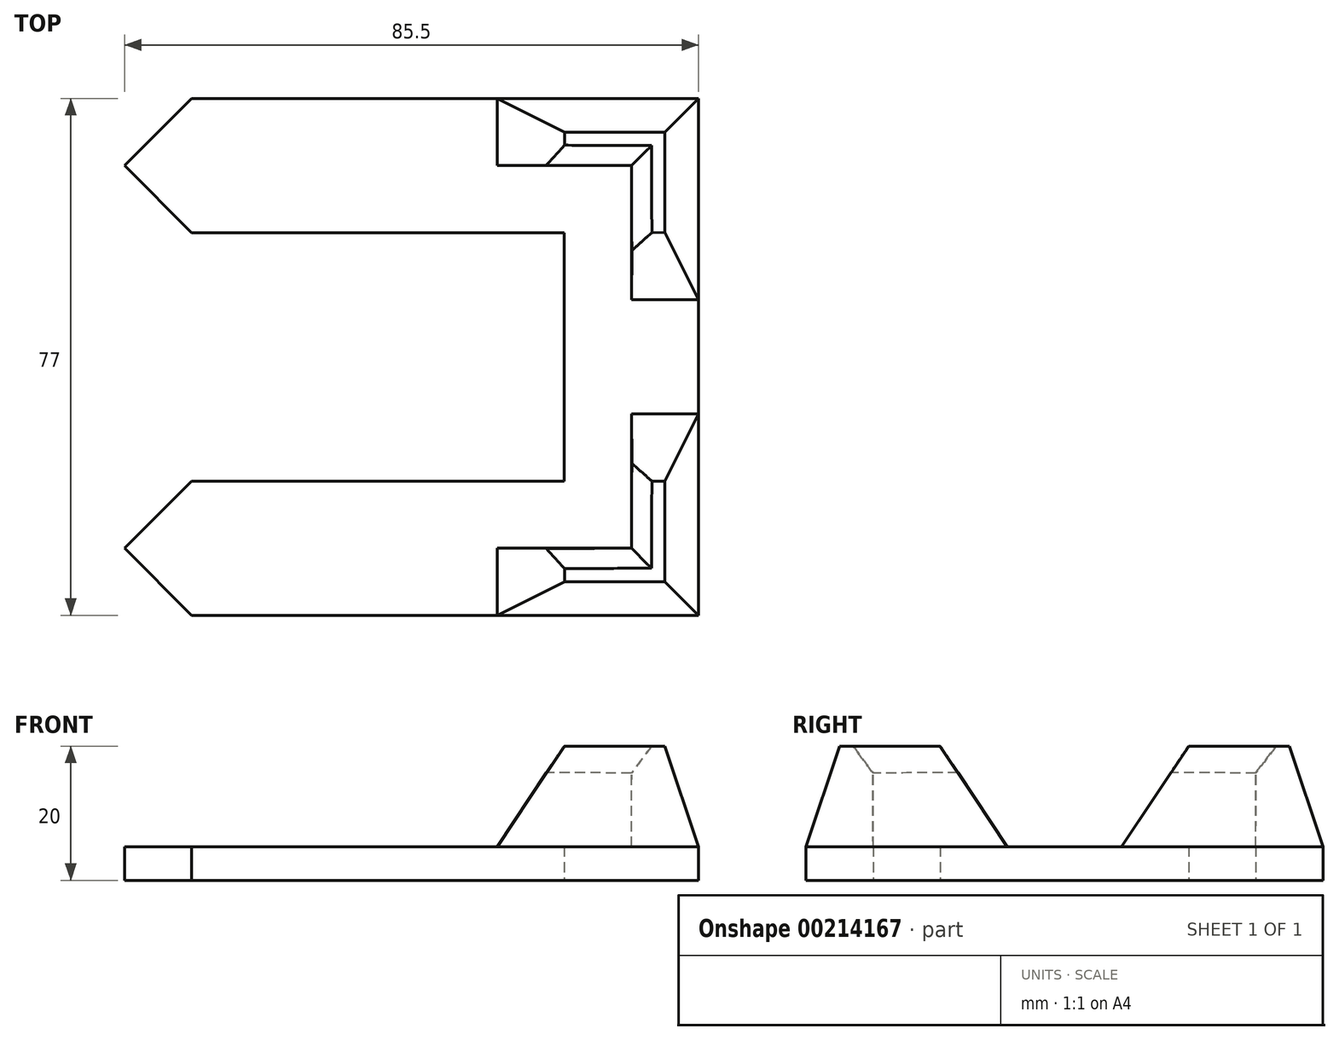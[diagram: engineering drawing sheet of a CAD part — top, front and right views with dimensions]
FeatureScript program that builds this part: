
annotation { "Feature Type Name" : "Feature", "Feature Type Description" : "" }
export const myFeature = defineFeature(function(context is Context, id is Id, definition is map)
    precondition{}
    {
        {
            var Q0;
            Q0=qCreatedBy(makeId("Top.planeOp"),FACE);
            var sketch = newSketch(context, id + "F0", { "sketchPlane" : qUnion([Q0])});
            skLineSegment(sketch, "E0.bottom", {"start": v(75.5, -28.5) * mm, "end": v(-75.5, -28.5) * mm, "construction": true});
            skLineSegment(sketch, "E0.top", {"start": v(75.5, 28.5) * mm, "end": v(-75.5, 28.5) * mm, "construction": true});
            skLineSegment(sketch, "E0.left", {"start": v(75.5, -28.5) * mm, "end": v(75.5, 28.5) * mm, "construction": true});
            skLineSegment(sketch, "E0.right", {"start": v(-75.5, -28.5) * mm, "end": v(-75.5, 28.5) * mm, "construction": true});
            skPoint(sketch, "E0.middle", {"position": v(0, 0) * mm});
            skLineSegment(sketch, "E1.bottom", {"start": v(85.5, -38.5) * mm, "end": v(-85.5, -38.5) * mm});
            skLineSegment(sketch, "E1.top", {"start": v(85.5, 38.5) * mm, "end": v(-85.5, 38.5) * mm});
            skLineSegment(sketch, "E1.left", {"start": v(85.5, -38.5) * mm, "end": v(85.5, 38.5) * mm});
            skLineSegment(sketch, "E1.right", {"start": v(-85.5, -38.5) * mm, "end": v(-85.5, 38.5) * mm});
            skSolve(sketch);
        }
        {
            var Q0;
            Q0=qCreatedBy(makeId("Top.planeOp"),FACE);
            cPlane(context, id + "F1", {"entities" : qUnion([Q0]), "cplaneType" : CPlaneType.OFFSET, "offset" : 15 * mm, "width" : 150 * mm, "height" : 150 * mm});
        }
        {
            var Q0;
            Q0=qCreatedBy(id+"F1.planeOp",FACE);
            var sketch = newSketch(context, id + "F2", { "sketchPlane" : qUnion([Q0])});
            skPoint(sketch, "E2.0", {"position": v(-85.5, -38.5) * mm});
            skPoint(sketch, "E3.0", {"position": v(-75.5, -28.5) * mm});
            skLineSegment(sketch, "E4", {"start": v(-75.58, -18.5) * mm, "end": v(-75.5, -28.5) * mm});
            skLineSegment(sketch, "E5", {"start": v(-75.5, -28.5) * mm, "end": v(-85.5, -38.5) * mm, "construction": true});
            skPoint(sketch, "E6", {"position": v(-80.5, -33.5) * mm});
            skLineSegment(sketch, "E7", {"start": v(-75.58, -18.5) * mm, "end": v(-80.5, -18.54) * mm});
            skLineSegment(sketch, "E8", {"start": v(-80.5, -18.54) * mm, "end": v(-80.5, -33.5) * mm});
            skLineSegment(sketch, "E9.MirrorCS", {"start": v(-65.54, -33.5) * mm, "end": v(-80.5, -33.5) * mm});
            skLineSegment(sketch, "E10.MirrorCS", {"start": v(-65.5, -28.58) * mm, "end": v(-65.54, -33.5) * mm});
            skLineSegment(sketch, "E11.MirrorCS", {"start": v(-65.5, -28.58) * mm, "end": v(-75.5, -28.5) * mm});
            skSolve(sketch);
        }
        {
            var Q0;
            Q0=qCreatedBy(makeId("Top.planeOp"),FACE);
            var sketch = newSketch(context, id + "F3", { "sketchPlane" : qUnion([Q0])});
            skPoint(sketch, "E12.0", {"position": v(-85.5, -38.5) * mm});
            skPoint(sketch, "E13.0", {"position": v(-75.5, -28.5) * mm});
            skLineSegment(sketch, "E14", {"start": v(-85.5, -38.5) * mm, "end": v(-85.5, -8.5) * mm});
            skLineSegment(sketch, "E15", {"start": v(-85.5, -8.5) * mm, "end": v(-75.5, -8.5) * mm});
            skLineSegment(sketch, "E16", {"start": v(-75.5, -8.5) * mm, "end": v(-75.5, -28.5) * mm});
            skLineSegment(sketch, "E17", {"start": v(-75.5, -28.5) * mm, "end": v(-85.5, -38.5) * mm, "construction": true});
            skLineSegment(sketch, "E18.MirrorCS", {"start": v(-55.5, -28.5) * mm, "end": v(-75.5, -28.5) * mm});
            skLineSegment(sketch, "E19.MirrorCS", {"start": v(-85.5, -38.5) * mm, "end": v(-55.5, -38.5) * mm});
            skLineSegment(sketch, "E20.MirrorCS", {"start": v(-55.5, -38.5) * mm, "end": v(-55.5, -28.5) * mm});
            skSolve(sketch);
        }
        {
            var Q0;
            Q0=makeQuery(id+"F0.imprint","IMPRINT",FACE,{"disambiguationData":[TD([[makeQuery(id+"F0.imprint","IMPRINT",EDGE,{"derivedFrom":sQuery(id+"F0.wireOp",EDGE,"E1.bottom")}),-1.0]])]});
            extrude(context, id + "F4", {"entities" : qUnion([Q0]), "oppositeDirection" : true, "depth" : 5 * mm});
        }
        {
            var Q1;
            Q1=makeQuery(id+"F3.imprint","IMPRINT",FACE,{"disambiguationData":[TD([[makeQuery(id+"F3.imprint","IMPRINT",EDGE,{"derivedFrom":sQuery(id+"F3.wireOp",EDGE,"E14")}),-1.0]])]});
            var Q2;
            Q2=makeQuery(id+"F2.imprint","IMPRINT",FACE,{"disambiguationData":[TD([[makeQuery(id+"F2.imprint","IMPRINT",EDGE,{"derivedFrom":sQuery(id+"F2.wireOp",EDGE,"E4")}),-1.0]])]});
            loft(context, id + "F5", {"operationType" : NewBodyOperationType.ADD, "sheetProfilesArray" : [{ "sheetProfileEntities" : qUnion([Q1]) }, { "sheetProfileEntities" : qUnion([Q2]) }]});
        }
        {
            var Q0;
            Q0=makeQuery(id+"F5.opLoft","MID_CAP_EDGE",EDGE,{"disambiguationData":[OSD([sQuery(id+"F2.wireOp",EDGE,"E4"),sQuery(id+"F2.wireOp",EDGE,"E7"),sQuery(id+"F2.wireOp",EDGE,"E11.MirrorCS")])],"capPos":1.0});
            var Q1;
            Q1=makeQuery(id+"F5.opLoft","MID_CAP_EDGE",EDGE,{"disambiguationData":[OSD([sQuery(id+"F2.wireOp",EDGE,"E4"),sQuery(id+"F2.wireOp",EDGE,"E10.MirrorCS"),sQuery(id+"F2.wireOp",EDGE,"E11.MirrorCS")])],"capPos":1.0});
            chamfer(context, id + "F6", {"entities" : qUnion([Q0, Q1]), "chamferType" : ChamferType.TWO_OFFSETS, "width1" : 3 * mm, "oppositeDirection" : false, "width2" : 4 * mm, "tangentPropagation" : true});
        }
        {
            var Q0;
            Q0=makeQuery(id+"F4.opExtrude","SWEPT_BODY",BODY,{"disambiguationData":[OSD([sQuery(id+"F0.wireOp",EDGE,"E1.bottom"),sQuery(id+"F0.wireOp",EDGE,"E1.top"),sQuery(id+"F0.wireOp",EDGE,"E1.left"),sQuery(id+"F0.wireOp",EDGE,"E1.right")])]});
            var Q1;
            Q1=qCreatedBy(makeId("Right.planeOp"),FACE);
            mirror(context, id + "F7", {"operationType" : NewBodyOperationType.ADD, "entities" : qUnion([Q0]), "mirrorPlane" : qUnion([Q1])});
        }
        {
            var Q0;
            Q0=makeQuery(id+"F4.opExtrude","SWEPT_BODY",BODY,{"disambiguationData":[OSD([sQuery(id+"F0.wireOp",EDGE,"E1.bottom"),sQuery(id+"F0.wireOp",EDGE,"E1.top"),sQuery(id+"F0.wireOp",EDGE,"E1.left"),sQuery(id+"F0.wireOp",EDGE,"E1.right")])]});
            var Q1;
            Q1=qCreatedBy(makeId("Front.planeOp"),FACE);
            mirror(context, id + "F8", {"operationType" : NewBodyOperationType.ADD, "entities" : qUnion([Q0]), "mirrorPlane" : qUnion([Q1])});
        }
        {
            var Q0;
            Q0=qCreatedBy(makeId("Top.planeOp"),FACE);
            var sketch = newSketch(context, id + "F9", { "sketchPlane" : qUnion([Q0])});
            skLineSegment(sketch, "E21.bottom", {"start": v(65.5, -18.5) * mm, "end": v(-65.5, -18.5) * mm});
            skLineSegment(sketch, "E21.top", {"start": v(65.5, 18.5) * mm, "end": v(-65.5, 18.5) * mm});
            skLineSegment(sketch, "E21.left", {"start": v(65.5, -18.5) * mm, "end": v(65.5, 18.5) * mm});
            skLineSegment(sketch, "E21.right", {"start": v(-65.5, -18.5) * mm, "end": v(-65.5, 18.5) * mm});
            skPoint(sketch, "E21.middle", {"position": v(0, 0) * mm});
            skLineSegment(sketch, "E22.0", {"start": v(-75.5, -28.5) * mm, "end": v(-75.5, 28.5) * mm, "construction": true});
            skLineSegment(sketch, "E23.0", {"start": v(75.5, 28.5) * mm, "end": v(-75.5, 28.5) * mm, "construction": true});
            skSolve(sketch);
        }
        {
            var Q0;
            Q0=qSketchRegion(id+"F9",true);
            extrude(context, id + "F10", {"entities" : qUnion([Q0]), "operationType" : NewBodyOperationType.REMOVE, "depth" : 25 * mm, "symmetric" : true});
        }
        {
            var Q0;
            Q0=makeQuery(id+"F0.imprint","IMPRINT",FACE,{"disambiguationData":[TD([[makeQuery(id+"F0.imprint","IMPRINT",EDGE,{"derivedFrom":sQuery(id+"F0.wireOp",EDGE,"E1.bottom")}),-1.0]])]});
            var sketch = newSketch(context, id + "F11", { "sketchPlane" : qUnion([Q0])});
            skLineSegment(sketch, "E24.0", {"start": v(75.5, 28.5) * mm, "end": v(-75.5, 28.5) * mm, "construction": true});
            skLineSegment(sketch, "E24.1", {"start": v(-65.5, 18.5) * mm, "end": v(65.5, 18.5) * mm, "construction": true});
            skLineSegment(sketch, "E24.2", {"start": v(85.5, 38.5) * mm, "end": v(-85.5, 38.5) * mm, "construction": true});
            skPoint(sketch, "E24.3", {"position": v(0, 28.5) * mm});
            skLineSegment(sketch, "E25", {"start": v(0, 28.5) * mm, "end": v(18.64, 9.86) * mm});
            skLineSegment(sketch, "E26", {"start": v(18.64, 9.86) * mm, "end": v(18.64, -9.86) * mm});
            skLineSegment(sketch, "E27", {"start": v(18.64, -9.86) * mm, "end": v(0, -28.5) * mm});
            skLineSegment(sketch, "E28", {"start": v(0, -28.5) * mm, "end": v(18.64, -47.14) * mm});
            skLineSegment(sketch, "E29", {"start": v(18.64, -47.14) * mm, "end": v(91.07, -47.14) * mm});
            skLineSegment(sketch, "E30", {"start": v(91.07, -47.14) * mm, "end": v(91.07, 44.05) * mm});
            skLineSegment(sketch, "E31", {"start": v(91.07, 44.05) * mm, "end": v(15.55, 44.05) * mm});
            skLineSegment(sketch, "E32", {"start": v(15.55, 44.05) * mm, "end": v(0, 28.5) * mm});
            skSolve(sketch);
        }
        {
            var Q0;
            {var subQ5=sQuery(id+"F11.wireOp",EDGE,"E25");Q0=makeQuery(id+"F11.imprint","IMPRINT",FACE,{"disambiguationData":[TD([[makeQuery(id+"F11.imprint","IMPRINT",EDGE,{"derivedFrom":subQ5}),1.0]])]});}
            var Q1;
            {var subQ1=sQuery(id+"F11.wireOp",EDGE,"E29");Q1=makeQuery(id+"F11.imprint","IMPRINT",FACE,{"disambiguationData":[TD([[makeQuery(id+"F11.imprint","IMPRINT",EDGE,{"derivedFrom":subQ1}),1.0]])]});}
            extrude(context, id + "F12", {"entities" : qUnion([Q0, Q1]), "depth" : 25 * mm, "hasSecondDirection" : true, "secondDirectionOppositeDirection" : true, "secondDirectionDepth" : 25 * mm});
        }
        {
            var Q0;
            Q0=makeQuery(id+"F12.opExtrude","SWEPT_BODY",BODY,{"disambiguationData":[OSD([sQuery(id+"F11.wireOp",EDGE,"E25"),sQuery(id+"F11.wireOp",EDGE,"E26"),sQuery(id+"F11.wireOp",EDGE,"E27"),sQuery(id+"F11.wireOp",EDGE,"E28"),sQuery(id+"F11.wireOp",EDGE,"E29"),sQuery(id+"F11.wireOp",EDGE,"E30"),sQuery(id+"F11.wireOp",EDGE,"E31"),sQuery(id+"F11.wireOp",EDGE,"E32")])]});
            var Q1;
            Q1=makeQuery(id+"F4.opExtrude","SWEPT_BODY",BODY,{"disambiguationData":[OSD([sQuery(id+"F0.wireOp",EDGE,"E1.bottom"),sQuery(id+"F0.wireOp",EDGE,"E1.top"),sQuery(id+"F0.wireOp",EDGE,"E1.left"),sQuery(id+"F0.wireOp",EDGE,"E1.right")])]});
            var Q2;
            Q2=makeQuery(id+"F4.opExtrude","SWEPT_BODY",BODY,{"disambiguationData":[OSD([sQuery(id+"F0.wireOp",EDGE,"E1.bottom"),sQuery(id+"F0.wireOp",EDGE,"E1.top"),sQuery(id+"F0.wireOp",EDGE,"E1.left"),sQuery(id+"F0.wireOp",EDGE,"E1.right")])]});
            booleanBodies(context, id + "F13", {"operationType" : BooleanOperationType.INTERSECTION, "tools" : qUnion([Q0, Q1]), "targets" : qUnion([Q2])});
        }
    });
